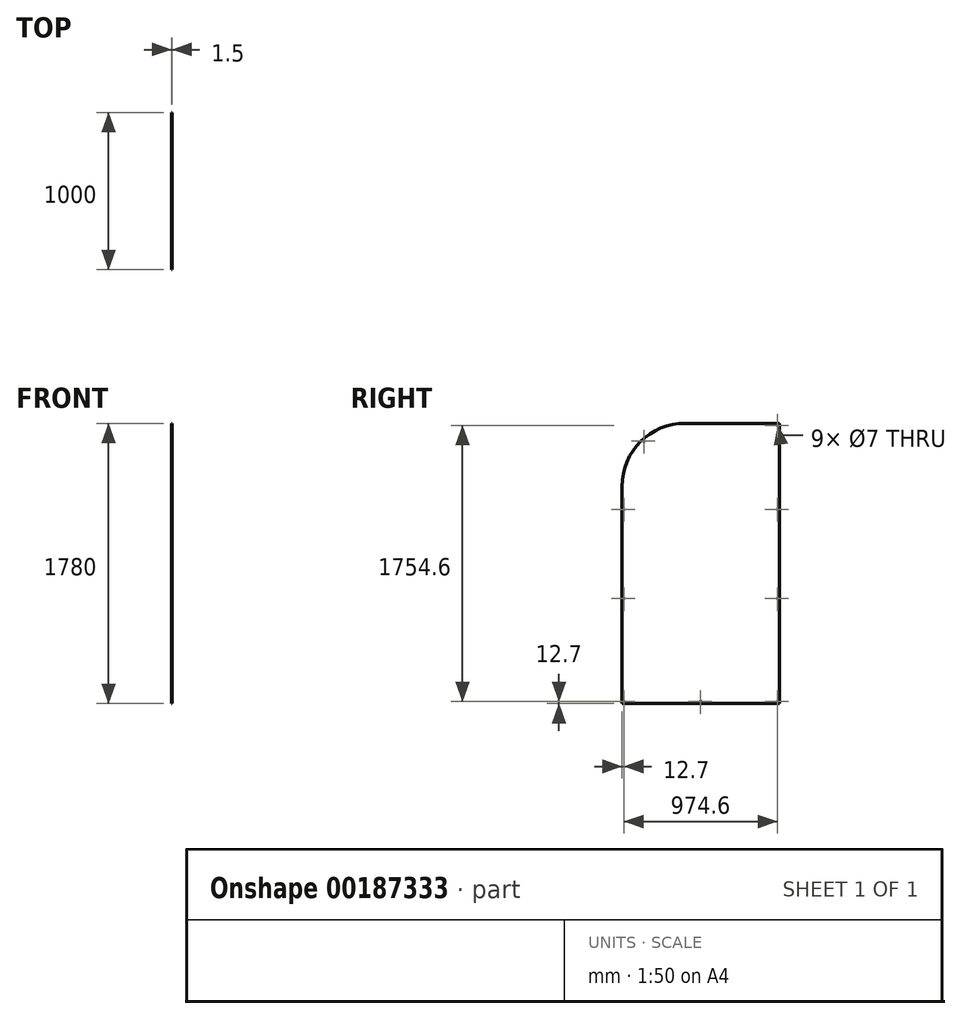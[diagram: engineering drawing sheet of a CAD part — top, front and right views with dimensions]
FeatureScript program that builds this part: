
annotation { "Feature Type Name" : "Feature", "Feature Type Description" : "" }
export const myFeature = defineFeature(function(context is Context, id is Id, definition is map)
    precondition{}
    {
        {
            var Q0;
            Q0=qCreatedBy(makeId("Right.planeOp"),FACE);
            var sketch = newSketch(context, id + "F0", { "sketchPlane" : qUnion([Q0])});
            skLineSegment(sketch, "E0.bottom", {"start": v(500, 890) * mm, "end": v(-100, 890) * mm});
            skLineSegment(sketch, "E0.top", {"start": v(500, -890) * mm, "end": v(-500, -890) * mm});
            skLineSegment(sketch, "E0.left", {"start": v(500, 890) * mm, "end": v(500, -890) * mm});
            skLineSegment(sketch, "E0.right", {"start": v(-500, 490) * mm, "end": v(-500, -890) * mm});
            skPoint(sketch, "E0.middle", {"position": v(0, 0) * mm});
            skPoint(sketch, "E1.visualSharp", {"position": v(-500, 890) * mm});
            skArc(sketch, "E1.filletArc", {"start": v(-100, 890) * mm, "mid": v(-382.84, 772.84) * mm, "end": v(-500, 490) * mm});
            skCircle(sketch, "E2", {"center": v(0, -877.3) * mm, "radius": 3.5 * mm});
            skCircle(sketch, "E3", {"center": v(-487.3, -877.3) * mm, "radius": 3.5 * mm});
            skCircle(sketch, "E4", {"center": v(487.3, -877.3) * mm, "radius": 3.5 * mm});
            skCircle(sketch, "E5", {"center": v(487.3, -222.65) * mm, "radius": 3.5 * mm});
            skCircle(sketch, "E6", {"center": v(-487.3, -222.65) * mm, "radius": 3.5 * mm});
            skCircle(sketch, "E7", {"center": v(487.3, 343.45) * mm, "radius": 3.5 * mm});
            skCircle(sketch, "E8", {"center": v(-487.3, 343.45) * mm, "radius": 3.5 * mm});
            skCircle(sketch, "E9", {"center": v(487.3, 877.3) * mm, "radius": 3.5 * mm});
            skCircle(sketch, "E10", {"center": v(-360.64, 776.47) * mm, "radius": 3.5 * mm});
            skSolve(sketch);
        }
        {
            var Q0;
            Q0=qSketchRegion(id+"F0",true);
            extrude(context, id + "F1", {"entities" : qUnion([Q0]), "endBound" : BoundingType.SYMMETRIC, "depth" : 1.5 * mm});
        }
    });
